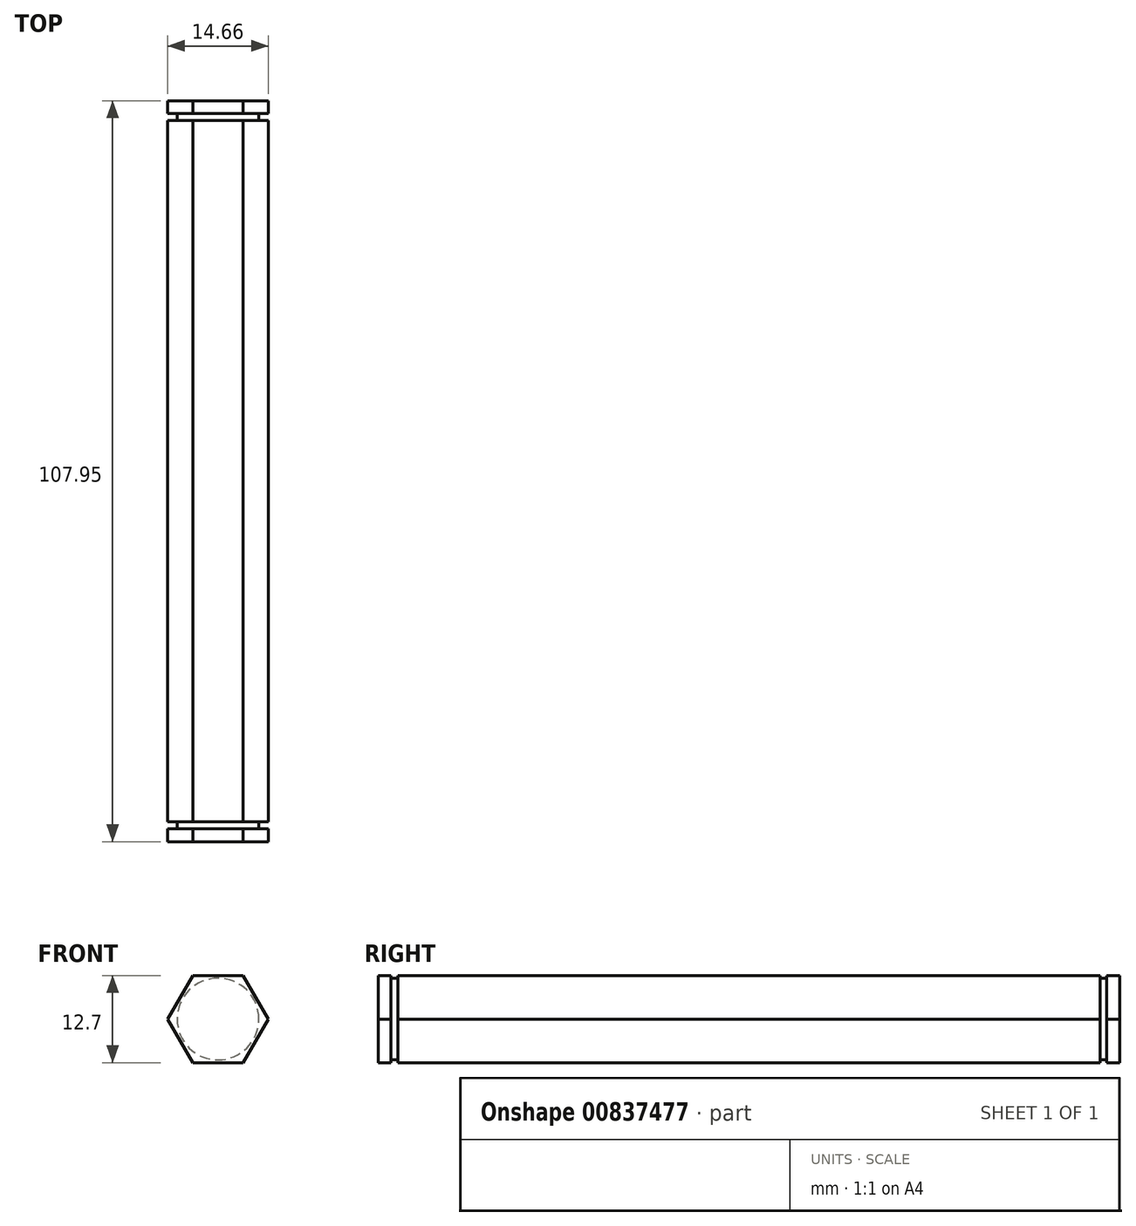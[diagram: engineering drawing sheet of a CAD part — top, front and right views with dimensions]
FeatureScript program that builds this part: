
annotation { "Feature Type Name" : "Feature", "Feature Type Description" : "" }
export const myFeature = defineFeature(function(context is Context, id is Id, definition is map)
    precondition{}
    {
        {
            var Q0;
            Q0=qCreatedBy(makeId("Front.planeOp"),FACE);
            var sketch = newSketch(context, id + "F0", { "sketchPlane" : qUnion([Q0])});
            skCircle(sketch, "E0.cCircle", {"center": v(0, 0) * mm, "radius": 6.35 * mm, "construction": true});
            skLineSegment(sketch, "E0.0", {"start": v(-3.67, 6.35) * mm, "end": v(3.67, 6.35) * mm});
            skLineSegment(sketch, "E0.1", {"start": v(3.67, 6.35) * mm, "end": v(7.33, 0) * mm});
            skLineSegment(sketch, "E0.2", {"start": v(7.33, 0) * mm, "end": v(3.67, -6.35) * mm});
            skLineSegment(sketch, "E0.3", {"start": v(3.67, -6.35) * mm, "end": v(-3.67, -6.35) * mm});
            skLineSegment(sketch, "E0.4", {"start": v(-3.67, -6.35) * mm, "end": v(-7.33, 0) * mm});
            skLineSegment(sketch, "E0.5", {"start": v(-7.33, 0) * mm, "end": v(-3.67, 6.35) * mm});
            skPoint(sketch, "E0.0.midPoint", {"position": v(0, 6.35) * mm});
            skSolve(sketch);
        }
        {
            var Q0;
            Q0=qSketchRegion(id+"F0",true);
            extrude(context, id + "F1", {"entities" : qUnion([Q0]), "depth" : 107.95 * mm, "offsetDistance" : 25.4 * mm});
        }
        {
            var Q0;
            Q0=qCreatedBy(makeId("Right.planeOp"),FACE);
            var sketch = newSketch(context, id + "F2", { "sketchPlane" : qUnion([Q0])});
            skLineSegment(sketch, "E1.bottom", {"start": v(-1.88, 56.74) * mm, "end": v(-2.87, 56.74) * mm});
            skLineSegment(sketch, "E1.top", {"start": v(-1.88, 5.94) * mm, "end": v(-2.87, 5.94) * mm});
            skLineSegment(sketch, "E1.left", {"start": v(-1.88, 56.74) * mm, "end": v(-1.88, 5.94) * mm});
            skLineSegment(sketch, "E1.right", {"start": v(-2.87, 56.74) * mm, "end": v(-2.87, 5.94) * mm});
            skLineSegment(sketch, "E2", {"start": v(-2.87, 5.94) * mm, "end": v(-105.08, 5.94) * mm, "construction": true});
            skLineSegment(sketch, "E3.bottom", {"start": v(-105.08, 5.94) * mm, "end": v(-106.07, 5.94) * mm});
            skLineSegment(sketch, "E3.top", {"start": v(-105.08, 56.74) * mm, "end": v(-106.07, 56.74) * mm});
            skLineSegment(sketch, "E3.left", {"start": v(-105.08, 5.94) * mm, "end": v(-105.08, 56.74) * mm});
            skLineSegment(sketch, "E3.right", {"start": v(-106.07, 5.94) * mm, "end": v(-106.07, 56.74) * mm});
            skLineSegment(sketch, "E4", {"start": v(-53.98, 5.94) * mm, "end": v(-53.98, 0) * mm, "construction": true});
            skLineSegment(sketch, "E5", {"start": v(0, 0) * mm, "end": v(-107.95, 0) * mm, "construction": true});
            skSolve(sketch);
        }
        {
            var Q0;
            Q0=qSketchRegion(id+"F2",true);
            var Q1;
            Q1=sQuery(id+"F2.wireOp",EDGE,"E5");
            revolve(context, id + "F3", {"operationType" : NewBodyOperationType.REMOVE, "surfaceOperationType" : NewSurfaceOperationType.NEW, "entities" : qUnion([Q0]), "axis" : qUnion([Q1]), "revolveType" : RevolveType.FULL, "oppositeDirection" : true});
        }
    });
